# Revit family: terra_edelstahl_245_641288_000_1_6448
name_source: partatom
category: Lighting Fixtures
units: mm (PartAtom-declared; Revit-internal decimal feet)

## family parameters
Cut with Voids When Loaded = No
Host = Face
Light Source = No
Part Type = Normal
Room Calculation Point = No
Round Connector Dimension = Use Diameter
Shared = No

## types (1)
- TERRA EDELSTAHL 245 (1 x LED Modul 840, 2200 lm, 4000)
    Apparent Load = 28 VA
    CIE Flux Codes = 51 74 86 0 100
    Color Rendering = 80
    Color Temperature = 4000
    Default Elevation = 1800 mm
    Description = Series: TERRA EDELSTAHL 245
In-ground luminaire for pedestrian areas. Housing made of corrosion-resistant die-cast aluminium, powder-coated. Marine grade stainless steel square shaped cover and screws. Flush mounted toughened glass. High-performance LED freeform mirror optics with 62° beam angle. Integral flexible power cord H07-RN8F. Use of in-ground support is necessary, please order chosen version for your application separately. 
Colour: stainless steel
Length: 245 mm
Width: 245 mm
Height: 2 mm
Lamp: LED
System power: 28 W
Rated luminous flux: 2200 lm
Luminous efficiency: 79 lm/W
Control gear: Converter not necessary
Protection class: I
Type of protection: IP 68
    Height = 0 mm  [stored 0 ft]
    Lamp = 1 x LED Modul 840
    Lamp Light Flux = 2200 lm
    Lamp count = 1
    Length = 245 mm
    Lifetime = 50000 h
    Luminous efficacy = 79 lm/W
    Manufacturer = RZB
    ModVariant = No
    Model = 641288.000.1
    Mounting Place = Floor
    Mounting Type = Recessed
    Number of Poles = 1
    OnlyDefault = Yes
    Power Factor = 1
    Product Name = TERRA EDELSTAHL 245
    Product group = Ground recessed luminaire
    ProductGroupID = 3381
    Protection Class = Protection class I
    Protection Degree = IP 68
    RLX_Detail_Level = 1
    RLX_Emergency_Light_Flux = 0 lm
    RLX_Emergency_Type = 0
    RLX_Emergency_Type_DB = No
    RlxData = <blob elided: 44965 chars, md5=be415610>
    Socket = socket
    Standby Power = 0 W
    System Light Flux = 2200 lm
    System Power = 28 W
    Type Comments = ALEA SPOT
    Type Image = 641287.000.jpg
    URL = http://relux.com
    VarID = ---
    Voltage = 230 V
    Voltage Range = 220-240 V
    Weight = 0.00 kg
    Width = 245 mm

note: [stored X ft] marks values corroborated as IEEE doubles in the binary element streams (Revit-internal decimal feet)

## geometry (parser evidence)
native form markers: Sweep x10
no freeform markers — native parametric forms only
